# Revit family: STH21710PTO_30
name_source: partatom
category: Luminárias
units: mm (PartAtom-declared; Revit-internal decimal feet)

## family parameters
Com base no plano de trabalho = Não
Compartilhado = Não
Corte com vazios quando carregada = Não
Cota do conector redondo = Utilizar diâmetro
Fonte luminosa = Sim
Manter orientação da anotação = Não
Ponto de cálculo do ambiente = Não
Sempre na vertical = Sim
Tipo de parte = Normal

## types (1)
- STH21710PTO/30 - PRETO - BIVOLT - 3000K - 430lm
    Altura = 0.5 m
    Arquivo de rede fotométrica = STELLA - STH21710PTO-30 - POSTE BALIZADOR FRANKFURT 1.ies
    Comprimento = 0.1 m
    Dimerização = Não dimerizável
    Elevação padrão = 0 m
    Estrutura = Al - Preto
    Fabricante = Stella
    Filtro de cor = 16777215
    Fluxo Luminoso = 430 lm
    Grau de proteção (IP) = IP65
    IRC (Índice de reprodução de cores) = >80
    Largura = 0.1 m
    Luminoso = Luminoso - 3000K
    Modelo = Frankfurt
    Potência = 7 W
    Referência = STH21710PTO/30
    Temperatura da cor (K) = 3000 K
    Tensão Elétrica = 100V-240V
    Troca de temperatura da cor de lâmpada com esmaecimento = <Nenhum>
    URL = https://stella.com.br
    Vidro = Vidro
    Ângulo de Abertura = 100°
    Ângulo de inclinação = 90.00°
